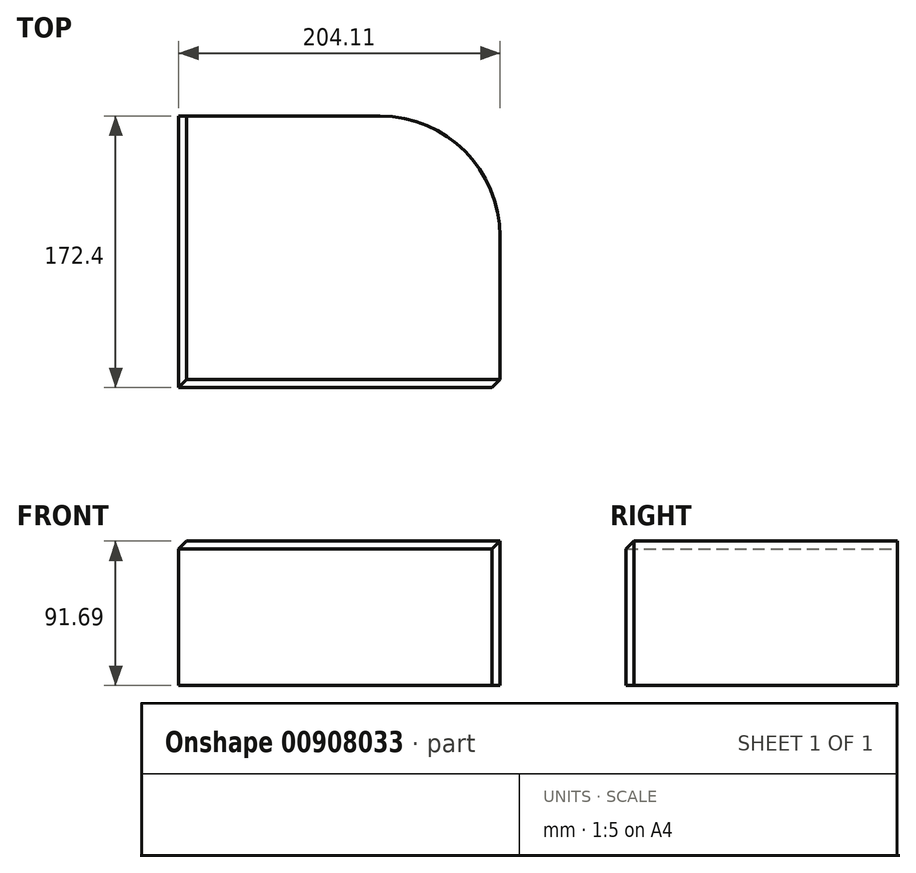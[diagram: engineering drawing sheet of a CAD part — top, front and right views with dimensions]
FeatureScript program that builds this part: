
annotation { "Feature Type Name" : "Feature", "Feature Type Description" : "" }
export const myFeature = defineFeature(function(context is Context, id is Id, definition is map)
    precondition{}
    {
        {
            var Q0;
            Q0=qCreatedBy(makeId("Top.planeOp"),FACE);
            var sketch = newSketch(context, id + "F0", { "sketchPlane" : qUnion([Q0])});
            skLineSegment(sketch, "E0.bottom", {"start": v(-72.22, 76.61) * mm, "end": v(131.89, 76.61) * mm});
            skLineSegment(sketch, "E0.top", {"start": v(-72.22, -95.79) * mm, "end": v(131.89, -95.79) * mm});
            skLineSegment(sketch, "E0.left", {"start": v(-72.22, 76.61) * mm, "end": v(-72.22, -95.79) * mm});
            skLineSegment(sketch, "E0.right", {"start": v(131.89, 76.61) * mm, "end": v(131.89, -95.79) * mm});
            skSolve(sketch);
        }
        {
            var Q0;
            Q0 = qSketchRegion(id + "F0", true);
            extrude(context, id + "F1", {"entities" : qUnion([Q0]), "depth" : 91.7 * mm, "offsetDistance" : 25.4 * mm});
        }
        {
            var Q0;
            Q0=makeQuery(id+"F1.opExtrude","CAP_EDGE",EDGE,{"disambiguationData":[OSD([sQuery(id+"F0.wireOp",EDGE,"E0.top")])],"isStart":false});
            var Q1;
            Q1=makeQuery(id+"F1.opExtrude","CAP_EDGE",EDGE,{"disambiguationData":[OSD([sQuery(id+"F0.wireOp",EDGE,"E0.left")])],"isStart":false});
            var Q2;
            Q2=makeQuery(id+"F1.opExtrude","SWEPT_EDGE",EDGE,{"disambiguationData":[OSD([sQuery(id+"F0.wireOp",EDGE,"E0.top"),sQuery(id+"F0.wireOp",EDGE,"E0.right")])]});
            chamfer(context, id + "F2", {"entities" : qUnion([Q0, Q1, Q2]), "width" : 5.08 * mm, "tangentPropagation" : true});
        }
        {
            var Q0;
            Q0=makeQuery(id+"F1.opExtrude","SWEPT_EDGE",EDGE,{"disambiguationData":[OSD([sQuery(id+"F0.wireOp",EDGE,"E0.bottom"),sQuery(id+"F0.wireOp",EDGE,"E0.right")])]});
            fillet(context, id + "F3", {"entities" : qUnion([Q0]), "radius" : 76.2 * mm, "tangentPropagation" : true, "allowEdgeOverflow" : false});
        }
    });
